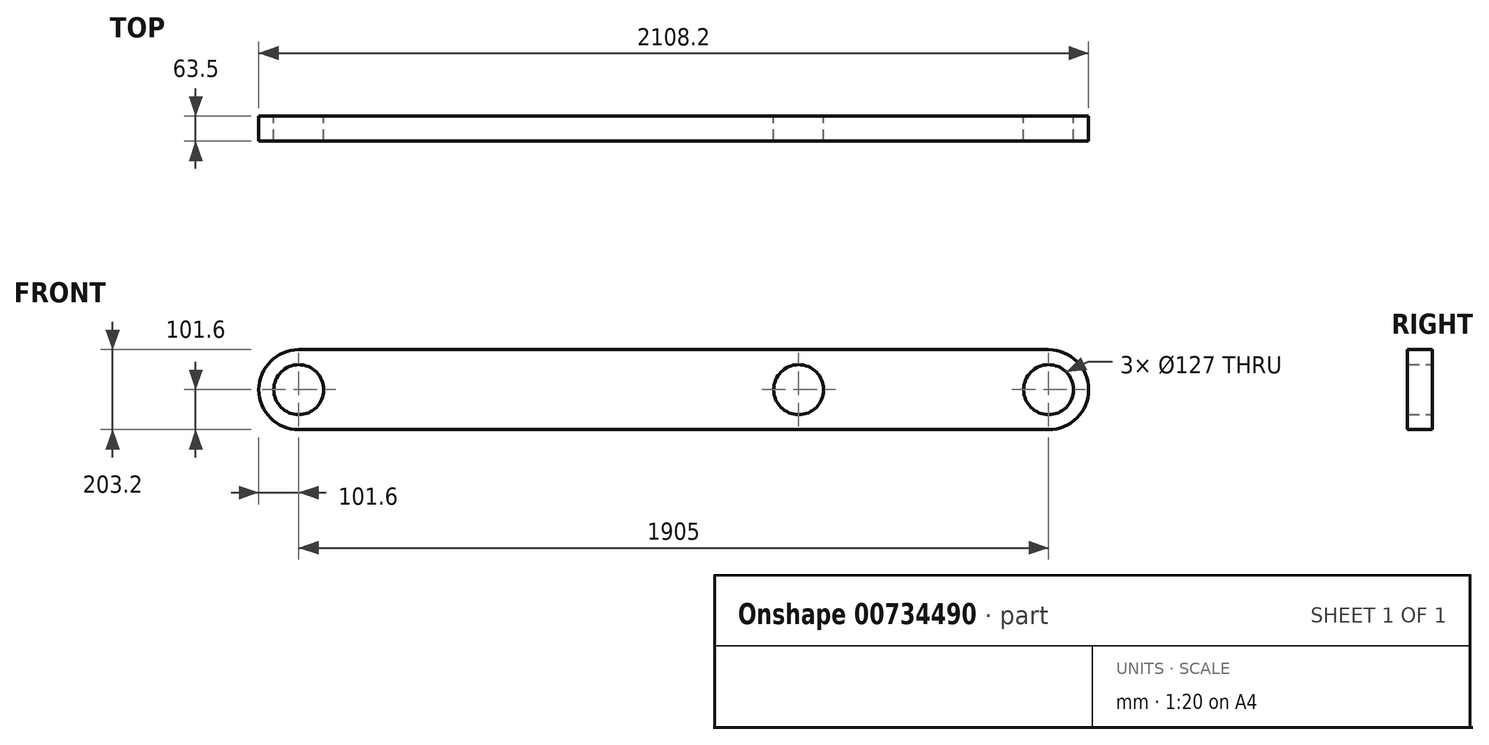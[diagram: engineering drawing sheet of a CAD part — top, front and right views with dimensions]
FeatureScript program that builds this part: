
annotation { "Feature Type Name" : "Feature", "Feature Type Description" : "" }
export const myFeature = defineFeature(function(context is Context, id is Id, definition is map)
    precondition{}
    {
        {
            var Q0;
            Q0=qCreatedBy(makeId("Front.planeOp"),FACE);
            var sketch = newSketch(context, id + "F0", { "sketchPlane" : qUnion([Q0])});
            skLineSegment(sketch, "E0", {"start": v(0, 0) * mm, "end": v(1905, 0) * mm, "construction": true});
            skArc(sketch, "E1", {"start": v(0, 101.6) * mm, "mid": v(-101.6, 0) * mm, "end": v(0, -101.6) * mm});
            skArc(sketch, "E2", {"start": v(1905, -101.6) * mm, "mid": v(2006.6, 0) * mm, "end": v(1905, 101.6) * mm});
            skLineSegment(sketch, "E3.0", {"start": v(0, -101.6) * mm, "end": v(1905, -101.6) * mm});
            skLineSegment(sketch, "E4.0", {"start": v(0, 101.6) * mm, "end": v(1905, 101.6) * mm});
            skCircle(sketch, "E5", {"center": v(0, 0) * mm, "radius": 63.5 * mm});
            skCircle(sketch, "E6", {"center": v(1905, 0) * mm, "radius": 63.5 * mm});
            skCircle(sketch, "E7", {"center": v(1270, 0) * mm, "radius": 63.5 * mm});
            skSolve(sketch);
        }
        {
            var Q0;
            Q0 = qSketchRegion(id + "F0", true);
            extrude(context, id + "F1", {"entities" : qUnion([Q0]), "depth" : 63.5 * mm, "offsetDistance" : 25.4 * mm});
        }
    });
